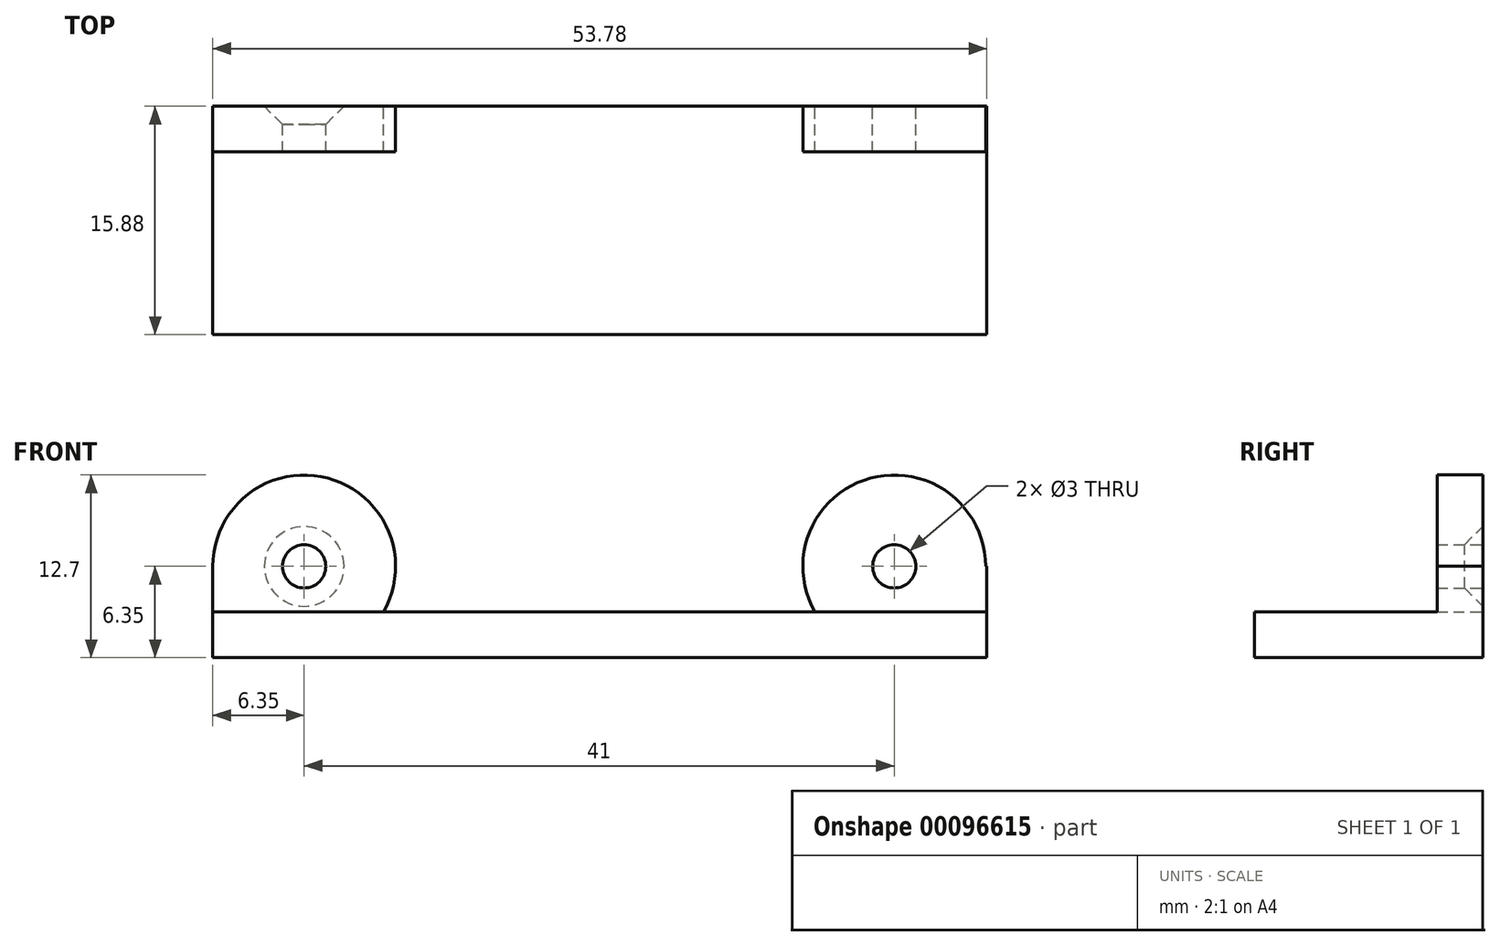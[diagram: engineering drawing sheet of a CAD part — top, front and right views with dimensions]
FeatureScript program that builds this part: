
annotation { "Feature Type Name" : "Feature", "Feature Type Description" : "" }
export const myFeature = defineFeature(function(context is Context, id is Id, definition is map)
    precondition{}
    {
        {
            var Q0;
            Q0=qCreatedBy(makeId("Front.planeOp"),FACE);
            var sketch = newSketch(context, id + "F0", { "sketchPlane" : qUnion([Q0])});
            skLineSegment(sketch, "E0", {"start": v(0, 0) * mm, "end": v(-41, 0) * mm});
            skLineSegment(sketch, "E1", {"start": v(-41, 0) * mm, "end": v(0, 0) * mm});
            skCircle(sketch, "E2", {"center": v(-41, 0) * mm, "radius": 1.5 * mm});
            skCircle(sketch, "E3", {"center": v(0, 0) * mm, "radius": 1.5 * mm});
            skCircle(sketch, "E4", {"center": v(-41, 0) * mm, "radius": 6.35 * mm});
            skCircle(sketch, "E5", {"center": v(0, 0) * mm, "radius": 6.35 * mm});
            skLineSegment(sketch, "E6", {"start": v(-40.78, 6.35) * mm, "end": v(0, 6.35) * mm});
            skLineSegment(sketch, "E7", {"start": v(0, 6.35) * mm, "end": v(-40.78, 6.35) * mm});
            skLineSegment(sketch, "E8.bottom", {"start": v(-47.35, 0) * mm, "end": v(6.43, 0) * mm});
            skLineSegment(sketch, "E8.top", {"start": v(-47.35, -3.18) * mm, "end": v(6.43, -3.18) * mm});
            skLineSegment(sketch, "E8.left", {"start": v(-47.35, 0) * mm, "end": v(-47.35, -3.18) * mm});
            skLineSegment(sketch, "E8.right", {"start": v(6.43, 0) * mm, "end": v(6.43, -3.18) * mm});
            skLineSegment(sketch, "E9.bottom", {"start": v(-51.67, -3.18) * mm, "end": v(10.94, -3.18) * mm});
            skLineSegment(sketch, "E9.top", {"start": v(-51.67, -6.35) * mm, "end": v(10.94, -6.35) * mm});
            skLineSegment(sketch, "E9.left", {"start": v(-51.67, -3.18) * mm, "end": v(-51.67, -6.35) * mm});
            skLineSegment(sketch, "E9.right", {"start": v(10.94, -3.18) * mm, "end": v(10.94, -6.35) * mm});
            skSolve(sketch);
        }
        {
            var Q0;
            {var subQ0=sQuery(id+"F0.wireOp",EDGE,"E8.bottom");var subQ3=sQuery(id+"F0.wireOp",EDGE,"E2");var subQ4=makeQuery(id+"F0.imprint","INTERSECT",VERTEX,{"disambiguationData":[OD(0.0)],"derivedFrom":[subQ3,subQ0]});Q0=makeQuery(id+"F0.imprint","IMPRINT",FACE,{"disambiguationData":[TD([[makeQuery(id+"F0.imprint","IMPRINT",EDGE,{"disambiguationData":[TD([[subQ4,1.0]])],"derivedFrom":subQ3}),-1.0]])]});}
            var Q1;
            {var subQ0=sQuery(id+"F0.wireOp",EDGE,"E7");var subQ1=sQuery(id+"F0.wireOp",EDGE,"E4");var subQ2=makeQuery(id+"F0.imprint","INTERSECT",VERTEX,{"derivedFrom":[subQ1,subQ0]});Q1=makeQuery(id+"F0.imprint","IMPRINT",FACE,{"disambiguationData":[TD([[makeQuery(id+"F0.imprint","IMPRINT",EDGE,{"disambiguationData":[TD([[subQ2,1.0]])],"derivedFrom":subQ1}),-1.0]])]});}
            var Q2;
            {var subQ0=sQuery(id+"F0.wireOp",EDGE,"E8.bottom");var subQ1=sQuery(id+"F0.wireOp",EDGE,"E2");var subQ2=makeQuery(id+"F0.imprint","INTERSECT",VERTEX,{"disambiguationData":[OD(0.0)],"derivedFrom":[subQ1,subQ0]});Q2=makeQuery(id+"F0.imprint","IMPRINT",FACE,{"disambiguationData":[TD([[makeQuery(id+"F0.imprint","IMPRINT",EDGE,{"disambiguationData":[TD([[subQ2,-1.0]])],"derivedFrom":subQ1}),-1.0]])]});}
            var Q3;
            {var subQ7=sQuery(id+"F0.wireOp",EDGE,"E8.left");Q3=makeQuery(id+"F0.imprint","IMPRINT",FACE,{"disambiguationData":[TD([[makeQuery(id+"F0.imprint","IMPRINT",EDGE,{"derivedFrom":subQ7}),1.0]])]});}
            var Q4;
            {var subQ0=sQuery(id+"F0.wireOp",EDGE,"E8.bottom");var subQ1=sQuery(id+"F0.wireOp",EDGE,"E3");var subQ2=makeQuery(id+"F0.imprint","INTERSECT",VERTEX,{"disambiguationData":[OD(0.0)],"derivedFrom":[subQ1,subQ0]});Q4=makeQuery(id+"F0.imprint","IMPRINT",FACE,{"disambiguationData":[TD([[makeQuery(id+"F0.imprint","IMPRINT",EDGE,{"disambiguationData":[TD([[subQ2,-1.0]])],"derivedFrom":subQ1}),-1.0]])]});}
            var Q5;
            {var subQ2=sQuery(id+"F0.wireOp",EDGE,"E8.bottom");var subQ5=sQuery(id+"F0.wireOp",EDGE,"E3");var subQ6=makeQuery(id+"F0.imprint","INTERSECT",VERTEX,{"disambiguationData":[OD(0.0)],"derivedFrom":[subQ5,subQ2]});Q5=makeQuery(id+"F0.imprint","IMPRINT",FACE,{"disambiguationData":[TD([[makeQuery(id+"F0.imprint","IMPRINT",EDGE,{"disambiguationData":[TD([[subQ6,1.0]])],"derivedFrom":subQ5}),-1.0]])]});}
            var Q6;
            Q6=makeQuery(id+"F0.imprint","IMPRINT",FACE,{"disambiguationData":[TD([[makeQuery(id+"F0.imprint","IMPRINT",EDGE,{"derivedFrom":sQuery(id+"F0.wireOp",EDGE,"E9.top")}),1.0]])]});
            var Q7;
            {var subQ4=sQuery(id+"F0.wireOp",EDGE,"E9.left");Q7=makeQuery(id+"F0.imprint","IMPRINT",FACE,{"disambiguationData":[TD([[makeQuery(id+"F0.imprint","IMPRINT",EDGE,{"derivedFrom":subQ4}),1.0]])]});}
            var Q8;
            {var subQ0=sQuery(id+"F0.wireOp",EDGE,"E4");var subQ1=makeQuery(id+"F0.imprint","INTERSECT",VERTEX,{"derivedFrom":[subQ0,sQuery(id+"F0.wireOp",EDGE,"E9.top")]});Q8=makeQuery(id+"F0.imprint","IMPRINT",FACE,{"disambiguationData":[TD([[makeQuery(id+"F0.imprint","IMPRINT",EDGE,{"disambiguationData":[TD([[subQ1,1.0]])],"derivedFrom":subQ0}),1.0]])]});}
            var Q9;
            {var subQ0=sQuery(id+"F0.wireOp",EDGE,"E8.bottom");var subQ1=sQuery(id+"F0.wireOp",EDGE,"E4");var subQ2=makeQuery(id+"F0.imprint","INTERSECT",VERTEX,{"derivedFrom":[subQ1,subQ0]});Q9=makeQuery(id+"F0.imprint","IMPRINT",FACE,{"disambiguationData":[TD([[makeQuery(id+"F0.imprint","IMPRINT",EDGE,{"disambiguationData":[TD([[subQ2,1.0]])],"derivedFrom":subQ1}),-1.0]])]});}
            var Q10;
            {var subQ0=sQuery(id+"F0.wireOp",EDGE,"E5");var subQ1=makeQuery(id+"F0.imprint","INTERSECT",VERTEX,{"derivedFrom":[subQ0,sQuery(id+"F0.wireOp",EDGE,"E9.top")]});Q10=makeQuery(id+"F0.imprint","IMPRINT",FACE,{"disambiguationData":[TD([[makeQuery(id+"F0.imprint","IMPRINT",EDGE,{"disambiguationData":[TD([[subQ1,1.0]])],"derivedFrom":subQ0}),1.0]])]});}
            var Q11;
            {var subQ0=sQuery(id+"F0.wireOp",EDGE,"E9.right");Q11=makeQuery(id+"F0.imprint","IMPRINT",FACE,{"disambiguationData":[TD([[makeQuery(id+"F0.imprint","IMPRINT",EDGE,{"derivedFrom":subQ0}),-1.0]])]});}
            var Q12;
            {var subQ5=sQuery(id+"F0.wireOp",EDGE,"E8.right");Q12=makeQuery(id+"F0.imprint","IMPRINT",FACE,{"disambiguationData":[TD([[makeQuery(id+"F0.imprint","IMPRINT",EDGE,{"derivedFrom":subQ5}),-1.0]])]});}
            extrude(context, id + "F1", {"entities" : qUnion([Q0, Q1, Q2, Q3, Q4, Q5, Q6, Q7, Q8, Q9, Q10, Q11, Q12]), "depth" : 3.17 * mm});
        }
        {
            var Q0;
            Q0=makeQuery(id+"F1.opExtrude","CAP_FACE",FACE,{"disambiguationData":[OSD([sQuery(id+"F0.wireOp",EDGE,"E2"),sQuery(id+"F0.wireOp",EDGE,"E3"),sQuery(id+"F0.wireOp",EDGE,"E4"),sQuery(id+"F0.wireOp",EDGE,"E5"),sQuery(id+"F0.wireOp",EDGE,"E7"),sQuery(id+"F0.wireOp",EDGE,"E8.bottom"),sQuery(id+"F0.wireOp",EDGE,"E8.left"),sQuery(id+"F0.wireOp",EDGE,"E8.right"),sQuery(id+"F0.wireOp",EDGE,"E9.bottom"),sQuery(id+"F0.wireOp",EDGE,"E9.top"),sQuery(id+"F0.wireOp",EDGE,"E9.left"),sQuery(id+"F0.wireOp",EDGE,"E9.right")])],"isStart":false});
            var sketch = newSketch(context, id + "F2", { "sketchPlane" : qUnion([Q0])});
            skLineSegment(sketch, "E10.bottom", {"start": v(-51.67, -3.18) * mm, "end": v(10.94, -3.18) * mm});
            skLineSegment(sketch, "E10.top", {"start": v(-51.67, -6.35) * mm, "end": v(10.94, -6.35) * mm});
            skLineSegment(sketch, "E10.left", {"start": v(-51.67, -3.18) * mm, "end": v(-51.67, -6.35) * mm});
            skLineSegment(sketch, "E10.right", {"start": v(10.94, -3.18) * mm, "end": v(10.94, -6.35) * mm});
            skSolve(sketch);
        }
        {
            var Q0;
            Q0 = qSketchRegion(id + "F2", true);
            extrude(context, id + "F3", {"entities" : qUnion([Q0]), "operationType" : NewBodyOperationType.ADD, "depth" : 12.7 * mm});
        }
        {
            var Q0;
            Q0=makeQuery(id+"F1.opExtrude","CAP_EDGE",EDGE,{"disambiguationData":[OSD([sQuery(id+"F0.wireOp",EDGE,"E2")])],"isStart":true});
            chamfer(context, id + "F4", {"entities" : qUnion([Q0]), "width" : 1.27 * mm, "tangentPropagation" : true});
        }
        {
            var Q0;
            Q0=makeQuery(id+"F3.boolean.opBoolean","MERGE",FACE,{"derivedFrom":[makeQuery(id+"F1.opExtrude","SWEPT_FACE",FACE,{"disambiguationData":[OSD([sQuery(id+"F0.wireOp",EDGE,"E9.right")])]}),makeQuery(id+"F3.opExtrude","SWEPT_FACE",FACE,{"disambiguationData":[OSD([sQuery(id+"F2.wireOp",EDGE,"E10.right")])]})]});
            var sketch = newSketch(context, id + "F5", { "sketchPlane" : qUnion([Q0])});
            skLineSegment(sketch, "E11.bottom", {"start": v(0, -6.35) * mm, "end": v(-15.88, -6.35) * mm});
            skLineSegment(sketch, "E11.top", {"start": v(0, -3.18) * mm, "end": v(-15.88, -3.18) * mm});
            skLineSegment(sketch, "E11.left", {"start": v(0, -6.35) * mm, "end": v(0, -3.18) * mm});
            skLineSegment(sketch, "E11.right", {"start": v(-15.88, -6.35) * mm, "end": v(-15.88, -3.18) * mm});
            skSolve(sketch);
        }
        {
            var Q0;
            Q0 = qSketchRegion(id + "F5", true);
            var Q1;
            Q1=makeQuery(id+"F1.opExtrude","SWEPT_FACE",FACE,{"disambiguationData":[OSD([sQuery(id+"F0.wireOp",EDGE,"E8.right")])]});
            extrude(context, id + "F6", {"entities" : qUnion([Q0]), "operationType" : NewBodyOperationType.REMOVE, "endBound" : BoundingType.UP_TO_SURFACE, "oppositeDirection" : true, "endBoundEntityFace" : qUnion([Q1]), "depth" : 25.4 * mm});
        }
        {
            var Q0;
            Q0=makeQuery(id+"F3.boolean.opBoolean","MERGE",FACE,{"derivedFrom":[makeQuery(id+"F1.opExtrude","SWEPT_FACE",FACE,{"disambiguationData":[OSD([sQuery(id+"F0.wireOp",EDGE,"E9.left")])]}),makeQuery(id+"F3.opExtrude","SWEPT_FACE",FACE,{"disambiguationData":[OSD([sQuery(id+"F2.wireOp",EDGE,"E10.left")])]})]});
            var sketch = newSketch(context, id + "F7", { "sketchPlane" : qUnion([Q0])});
            skLineSegment(sketch, "E12.bottom", {"start": v(0, -3.18) * mm, "end": v(15.88, -3.18) * mm});
            skLineSegment(sketch, "E12.top", {"start": v(0, -6.35) * mm, "end": v(15.88, -6.35) * mm});
            skLineSegment(sketch, "E12.left", {"start": v(0, -3.18) * mm, "end": v(0, -6.35) * mm});
            skLineSegment(sketch, "E12.right", {"start": v(15.88, -3.18) * mm, "end": v(15.88, -6.35) * mm});
            skSolve(sketch);
        }
        {
            var Q0;
            Q0 = qSketchRegion(id + "F7", true);
            var Q1;
            Q1=makeQuery(id+"F1.opExtrude","SWEPT_FACE",FACE,{"disambiguationData":[OSD([sQuery(id+"F0.wireOp",EDGE,"E8.left")])]});
            extrude(context, id + "F8", {"entities" : qUnion([Q0]), "operationType" : NewBodyOperationType.REMOVE, "endBound" : BoundingType.UP_TO_SURFACE, "oppositeDirection" : true, "endBoundEntityFace" : qUnion([Q1]), "depth" : 25.4 * mm});
        }
    });
